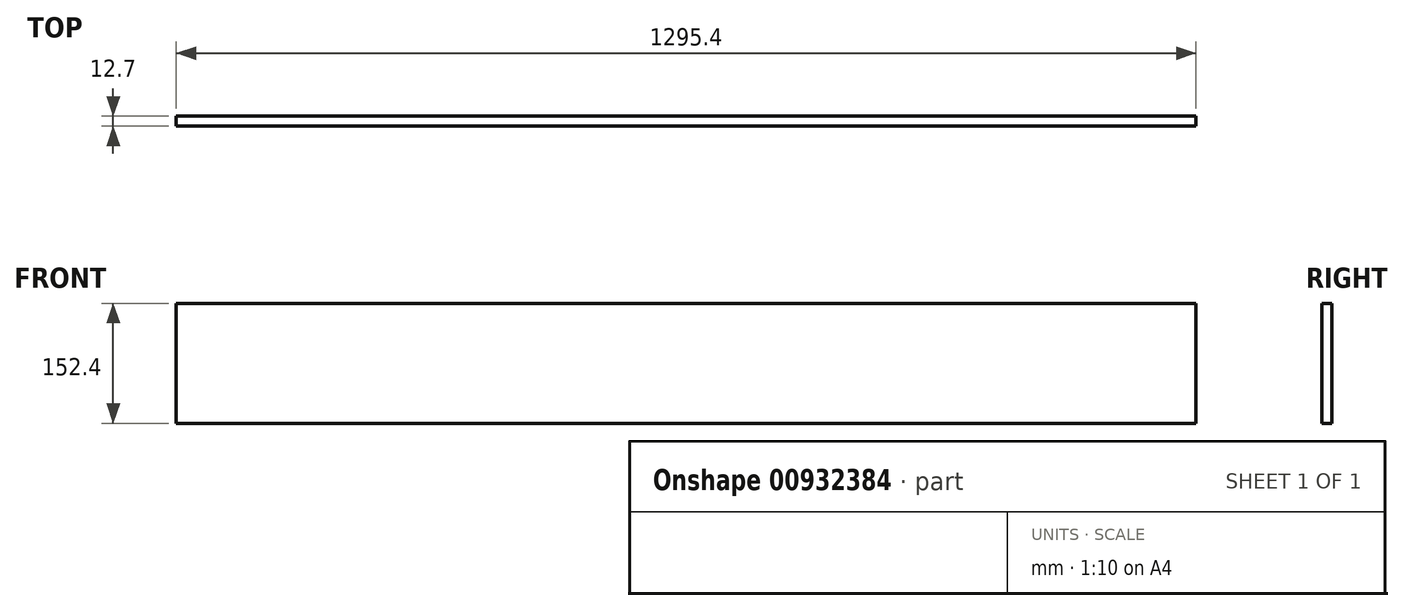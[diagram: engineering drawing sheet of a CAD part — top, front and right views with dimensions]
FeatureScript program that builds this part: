
annotation { "Feature Type Name" : "Feature", "Feature Type Description" : "" }
export const myFeature = defineFeature(function(context is Context, id is Id, definition is map)
    precondition{}
    {
        {
            var Q0;
            Q0=qCreatedBy(makeId("Front.planeOp"),FACE);
            var sketch = newSketch(context, id + "F0", { "sketchPlane" : qUnion([Q0])});
            skLineSegment(sketch, "E0.bottom", {"start": v(647.7, 76.2) * mm, "end": v(-647.7, 76.2) * mm});
            skLineSegment(sketch, "E0.top", {"start": v(647.7, -76.2) * mm, "end": v(-647.7, -76.2) * mm});
            skLineSegment(sketch, "E0.left", {"start": v(647.7, 76.2) * mm, "end": v(647.7, -76.2) * mm});
            skLineSegment(sketch, "E0.right", {"start": v(-647.7, 76.2) * mm, "end": v(-647.7, -76.2) * mm});
            skPoint(sketch, "E0.middle", {"position": v(0, 0) * mm});
            skSolve(sketch);
        }
        {
            var Q0;
            Q0=makeQuery(id+"F0.imprint","IMPRINT",FACE,{"disambiguationData":[TD([[makeQuery(id+"F0.imprint","IMPRINT",EDGE,{"derivedFrom":sQuery(id+"F0.wireOp",EDGE,"E0.bottom")}),1.0]])]});
            extrude(context, id + "F1", {"entities" : qUnion([Q0]), "depth" : 12.7 * mm, "offsetDistance" : 25.4 * mm});
        }
    });
